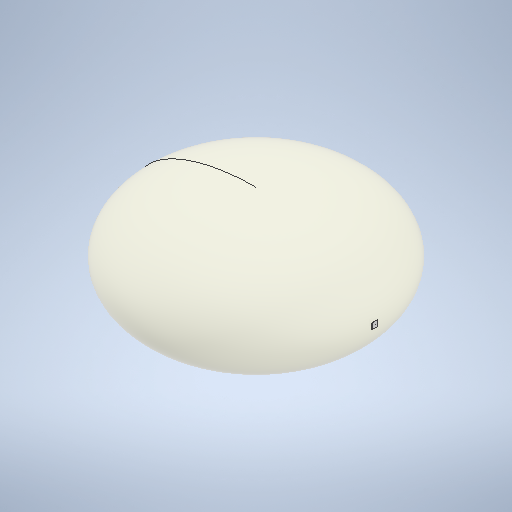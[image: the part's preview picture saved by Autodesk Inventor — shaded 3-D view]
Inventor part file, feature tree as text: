
AUTODESK INVENTOR PART (.ipt)
format: ipt  version: 2025 (Build 290162010, 162A)  size: 497,664 bytes
history: native  units: mm
features: other x4, sketch x3, extrude x2, revolve x1, pattern_circular x1
ambient origin geometry x8: Origin, YZ Plane, XZ Plane, XY Plane, X Axis, Y Axis, Z Axis, Center Point
bodies: Body1 (feature_tree)
feature tree (11):
  other  "솔리드1"
  revolve  "회전1"
  other  "작업 평면1"
  extrude  "돌출1"  Depth=5000.0mm
  other  "작업 평면2"
  extrude  "돌출2"  TaperAngle=90.0deg  [1 undecoded]
  pattern_circular  "원형 패턴1"  [2 undecoded]
  sketch  "스케치1"
  other  "2D 방정식 곡선1"
  sketch  "스케치2"
  sketch  "스케치3"
note: 3 required parameter values undecoded (feature->parameter linkage not recoverable at this tier; creation-order binding heuristic only, values carry confidence <= 0.55)
